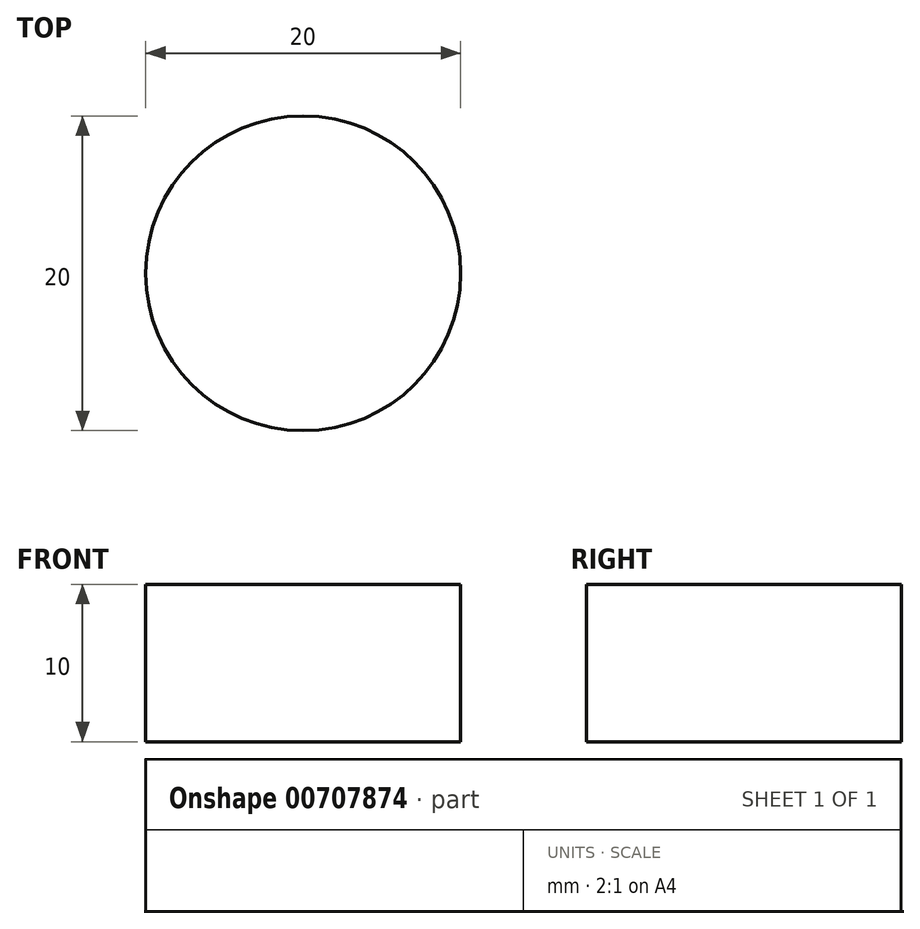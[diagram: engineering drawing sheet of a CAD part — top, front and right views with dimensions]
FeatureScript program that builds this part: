
annotation { "Feature Type Name" : "Feature", "Feature Type Description" : "" }
export const myFeature = defineFeature(function(context is Context, id is Id, definition is map)
    precondition{}
    {
        {
            var Q0;
            Q0=qCreatedBy(makeId("Top.planeOp"),FACE);
            var sketch = newSketch(context, id + "F0", { "sketchPlane" : qUnion([Q0])});
            skCircle(sketch, "E0", {"center": v(0, 0) * mm, "radius": 10 * mm});
            skCircle(sketch, "E1", {"center": v(0, 0) * mm, "radius": 5 * mm});
            skSolve(sketch);
        }
        {
            var Q0;
            Q0=qCreatedBy(makeId("Front.planeOp"),FACE);
            var sketch = newSketch(context, id + "F1", { "sketchPlane" : qUnion([Q0])});
            skSolve(sketch);
        }
        {
            var Q0;
            Q0=sQuery(id+"F0.wireOp",EDGE,"E0");
            var Q1;
            Q1 = qConstructionFilter(qBodyType(qCreatedBy(id + "F1" ,EDGE), BodyType.WIRE), ConstructionObject.NO);
            extrude(context, id + "F2", {"bodyType" : ToolBodyType.SURFACE, "surfaceEntities" : qUnion([Q0, Q1]), "depth" : 10 * mm, "offsetDistance" : 25 * mm});
        }
    });
